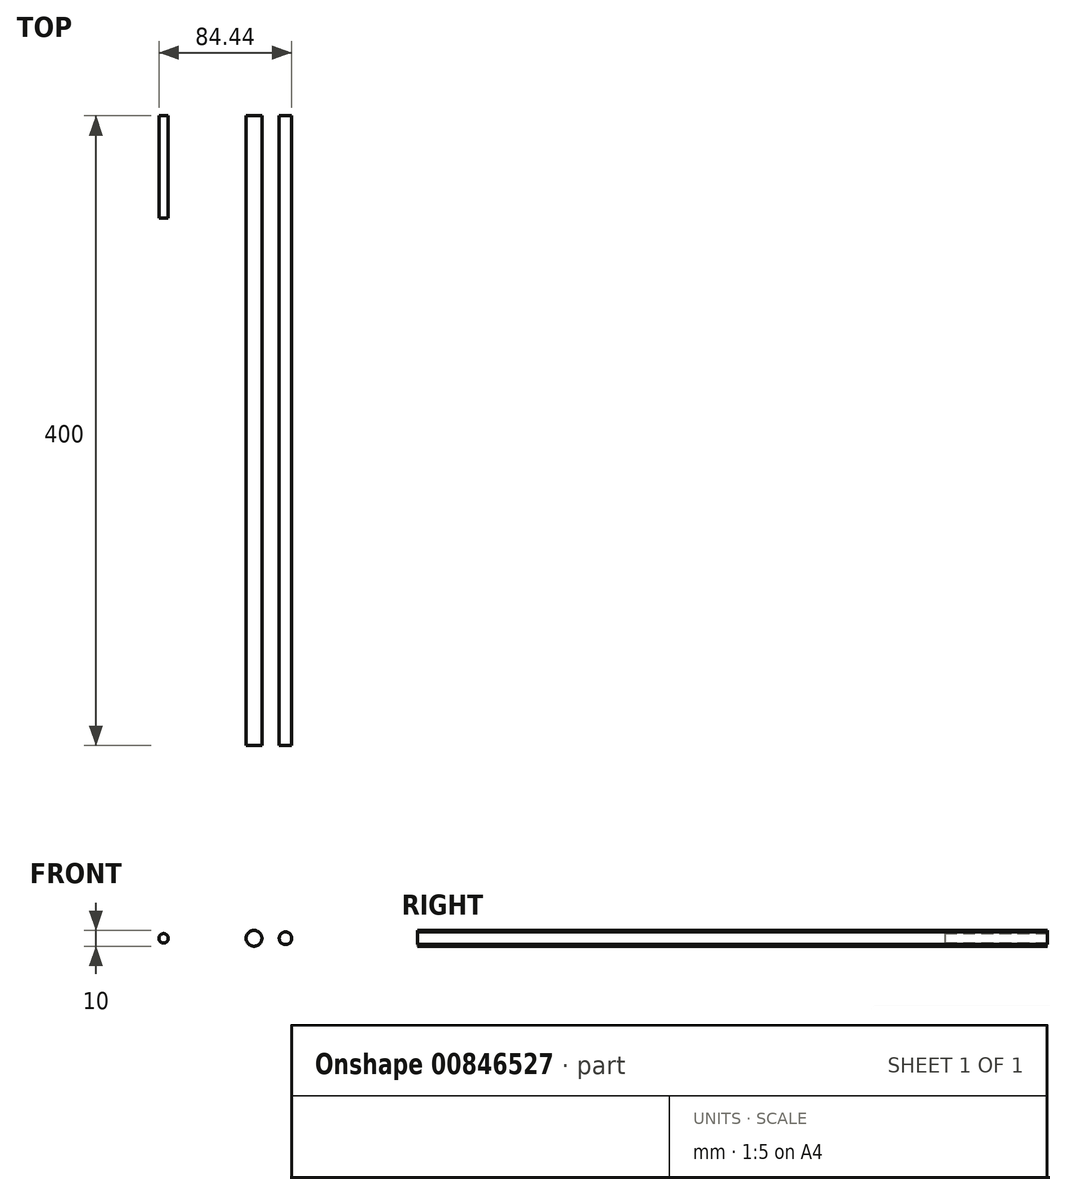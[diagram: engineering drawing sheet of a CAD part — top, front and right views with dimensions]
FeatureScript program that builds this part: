
annotation { "Feature Type Name" : "Feature", "Feature Type Description" : "" }
export const myFeature = defineFeature(function(context is Context, id is Id, definition is map)
    precondition{}
    {
        {
            var Q0;
            Q0=qCreatedBy(makeId("Front.planeOp"),FACE);
            var sketch = newSketch(context, id + "F0", { "sketchPlane" : qUnion([Q0])});
            skCircle(sketch, "E0", {"center": v(0, 0) * mm, "radius": 5 * mm});
            skSolve(sketch);
        }
        {
            var Q0;
            Q0=qSketchRegion(id+"F0",true);
            extrude(context, id + "F1", {"entities" : qUnion([Q0]), "depth" : 400 * mm, "offsetDistance" : 25 * mm});
        }
        {
            var Q0;
            Q0=qCreatedBy(makeId("Front.planeOp"),FACE);
            var sketch = newSketch(context, id + "F2", { "sketchPlane" : qUnion([Q0])});
            skCircle(sketch, "E1", {"center": v(20, 0) * mm, "radius": 4 * mm});
            skSolve(sketch);
        }
        {
            var Q0;
            Q0=qSketchRegion(id+"F2",true);
            extrude(context, id + "F3", {"entities" : qUnion([Q0]), "depth" : 400 * mm, "offsetDistance" : 25 * mm});
        }
        {
            var Q0;
            Q0=qCreatedBy(makeId("Front.planeOp"),FACE);
            var sketch = newSketch(context, id + "F4", { "sketchPlane" : qUnion([Q0])});
            skCircle(sketch, "E2", {"center": v(-57.44, 0) * mm, "radius": 3 * mm});
            skSolve(sketch);
        }
        {
            var Q0;
            Q0=qSketchRegion(id+"F4",true);
            extrude(context, id + "F5", {"entities" : qUnion([Q0]), "depth" : 65 * mm, "offsetDistance" : 25 * mm});
        }
    });
